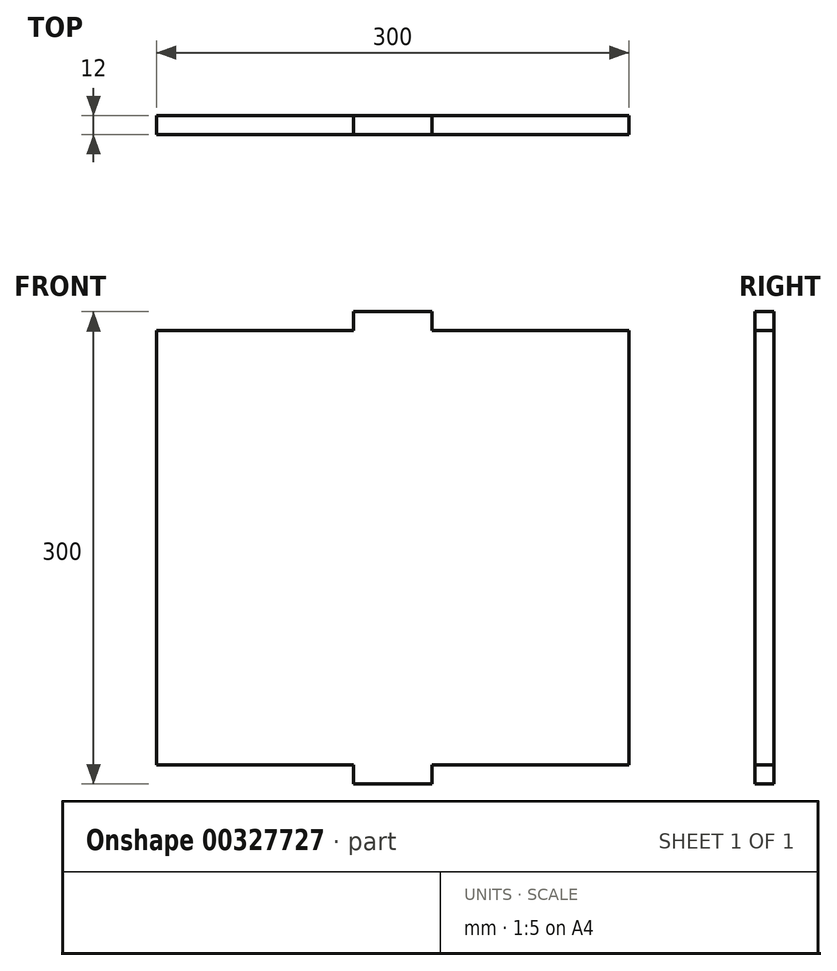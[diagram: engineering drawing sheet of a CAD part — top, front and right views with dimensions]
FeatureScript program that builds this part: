
annotation { "Feature Type Name" : "Feature", "Feature Type Description" : "" }
export const myFeature = defineFeature(function(context is Context, id is Id, definition is map)
    precondition{}
    {
        {
            var Q0;
            Q0=qCreatedBy(makeId("Front.planeOp"),FACE);
            var sketch = newSketch(context, id + "F0", { "sketchPlane" : qUnion([Q0])});
            skLineSegment(sketch, "E0.left", {"start": v(-187.56, 196.5) * mm, "end": v(-187.56, -79.5) * mm});
            skLineSegment(sketch, "E1", {"start": v(-187.56, -79.5) * mm, "end": v(-62.56, -79.5) * mm});
            skLineSegment(sketch, "E2", {"start": v(112.44, -79.5) * mm, "end": v(112.44, 196.5) * mm});
            skLineSegment(sketch, "E3", {"start": v(-62.56, 208.5) * mm, "end": v(-62.56, 196.5) * mm});
            skLineSegment(sketch, "E4", {"start": v(-12.56, 196.5) * mm, "end": v(-12.56, 208.5) * mm});
            skLineSegment(sketch, "E5", {"start": v(-62.56, 208.5) * mm, "end": v(-12.56, 208.5) * mm});
            skLineSegment(sketch, "E6", {"start": v(-62.56, 196.5) * mm, "end": v(-187.56, 196.5) * mm});
            skLineSegment(sketch, "E7", {"start": v(-12.56, 196.5) * mm, "end": v(112.44, 196.5) * mm});
            skLineSegment(sketch, "E8", {"start": v(-62.56, -79.5) * mm, "end": v(-62.56, -91.5) * mm});
            skLineSegment(sketch, "E9", {"start": v(-62.56, -91.5) * mm, "end": v(-12.56, -91.5) * mm});
            skLineSegment(sketch, "E10", {"start": v(-12.56, -91.5) * mm, "end": v(-12.56, -79.5) * mm});
            skLineSegment(sketch, "E11.trimOffspring", {"start": v(-12.56, -79.5) * mm, "end": v(112.44, -79.5) * mm});
            skSolve(sketch);
        }
        {
            var Q0;
            Q0 = qSketchRegion(id + "F0", true);
            extrude(context, id + "F1", {"entities" : qUnion([Q0]), "depth" : 12 * mm});
        }
    });
